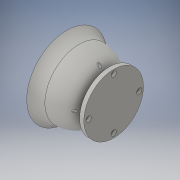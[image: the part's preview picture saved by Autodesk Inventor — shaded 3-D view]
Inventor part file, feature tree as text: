
AUTODESK INVENTOR PART (.ipt)
format: ipt  version: 2016 (Build 200138000, 138)  size: 251,392 bytes
history: native  units: in
note: dims shown in document units (in); Inventor stores cm internally (conversion verified against a paired STEP export)
features: hole x4, revolve x1, sketch x1
ambient origin geometry x8: Origin, YZ Plane, XZ Plane, XY Plane, X Axis, Y Axis, Z Axis, Center Point
bodies: Solid1 (feature_tree)
feature tree (6):
  revolve  "Revolution1"  [1 undecoded]
  hole  "Hole1"  [1 undecoded]
  hole  "Hole2"  [1 undecoded]
  hole  "Hole3"  [1 undecoded]
  hole  "Hole4"  [1 undecoded]
  sketch  "Sketch1"  dims[d0=1.9in d2=0.1in d3=0.125in d13=0.25in d14=1.75in d15=1.022in d16=1.1663in d17=2.3484in d18=2.1856in d19=2.2794in d20=1.9925in d21=0.1in d22=90.0deg d23=1.0in d24=1.0in d25=0.177in d26=0.75in d27=0.313in d28=0.164in d29=0.5635in d30=0.2547in d31=0.8108in d32=1.0in d33=1.0in d34=0.177in d35=0.75in d36=0.313in d37=0.164in d38=0.5635in d39=0.2547in d40=0.8108in d41=1.0in d42=1.0in d43=0.177in d44=0.75in d45=0.313in d46=0.164in d47=0.5635in d48=0.2547in d49=0.8108in d50=1.0in d51=1.0in d52=0.177in d53=0.75in d54=0.313in d55=0.164in d56=0.5635in d57=0.2547in d58=0.8108in]
note: 5 required parameter values undecoded (feature->parameter linkage not recoverable at this tier; creation-order binding heuristic only, values carry confidence <= 0.55)